# Revit family: OWIZVL 12'
name_source: partatom
category: Mechanical Equipment
units: mm (PartAtom-declared; Revit-internal decimal feet)

## family parameters
Always vertical = Yes
Cut with Voids When Loaded = No
OmniClass Number = 23.40.40.11.17
OmniClass Title = Refrigerated Cases
Part Type = Normal
Room Calculation Point = No
Round Connector Dimension = Use Radius
Shared = No
Work Plane-Based = Yes

## types (3) — shared parameters
Case Type/Application = Medium Temp
Certifications = NSF 7, UL471, CSA
DATE = 12-14-2015
DESIGNERS NAME = SHIDDRAMESH
Default Elevation = 48"
Description = OWIZV-Gaint Eagel
EQUIPMENT DESCRIPTION = OWIZV-Gaint Eagel
EQUIPMENT MARK = OWIZV- 7BF
GLASS = Glass
Height = 38 1/8"
High Power (Cornice) Amps = 1 A
How Many Defrosts Per Day = 1
Island Application = Frozen Food
Island BTUH Conventional = 610
Island BTUH Parallel = 587
Island Discharge Air Velocity (FPM) = 180 FPM
Island Discharge Air(°F) = -6 °F
Island Electric Fail-Safe = 60 (Min)
Island Electric Run-Off Time (Min) = 0 (Min)
Island Electric Termination Temp (F°) = 49 °F
Island Evaporator (°F) = -12 °F
Island High Efficiency Fans Amps = 0 A
Island Hot Gas Fail-Safe (Min) = 10 (Min)
Island Hot Gas Run-Off Time (Min) = 0 (Min)
Island Hot Gas Termination Temp (F°) = 60 °F
Island Superheat @ Bulb Set Point (°F) = 3-5 °F
Island Tank/Drain Heater Amps = 0 A
Island Tank/Drain Heater Watts = 30 W
Island Timed-Off Fail-Safe (Min) = 35 (Min)
Island Timed-Off Termination Temp (°F) = 42 °F
Item Description = OWIZV-Gaint Eagel
Legend Number = OWIZV- 7BF
Manufacturer = HILL PHOENIX
Model = OWIZV- 7BF
PAINTED METAL UPPER SHELF = PAINTED SHELVES
REF PLANE LEFT RIGHT = 41 7/16"
REFRIGERATION PIPING = COPPER PIPE
SHELF 10" = No
SHELF 16" = No
STAINLESS STEEL = GALVANIZED STEEL
SUPERSTRUCTURE 48" = No
SUPERSTRUCTURE 52" = No
SUPERSTRUCTURE 60" = No
Slider Lid = Slider Lids - 1 : Slider Lids
URL = http://www.hillphoenix.com
Width = 82 7/8"

## per-type parameters (varying)
| type | 12' Slider Lid | 6' lid | 8' lid | CENTER LINE | High Power (Cornice) Watts | Island  Case Length | Island 208V Defrost Heaters Amps | Island 208V Defrost Heaters Watts | Island 240 Defrost Heaters Amps | Island 240 Defrost Heaters Watts | Island Anti-Condensate Heaters Amps | Island Anti-Condensate Heaters Watts | Island Fans Per Case | Island High Efficiency Fans Watts | Length | Light Length | Lights Per Row | Standard Power Amps | Standard Power Watts |
| 06' - Frozen Food - Glass Front | No | Yes | No | 36" | 60 W | 72" | 9 A | 1800 A | 10 A | 2400 W | 2 A | 222 W | 4 | 16 W | 72" | 2-3' | 4 | 0 A | 33 W |
| 08' - Frozen Food - Glass  Front | No | No | Yes | 48" | 86 W | 96" | 12 A | 2400 A | 13 A | 3198 W | 1 A | 68 W | 4 | 16 W | 96" | 4-4' | 4 | 0 A | 48 W |
| 12' - Frozen Food - Glass Front | Yes | No | No | 72" | 129 W | 144" | 17 A | 3600 A | 20 A | 4795 W | 4 A | 454 W | 6 | 24 W | 144" | 3-4' | 6 | 1 A | 71 W |

## geometry (parser evidence)
native form markers: Blend x16, Sweep x9
no freeform markers — native parametric forms only
